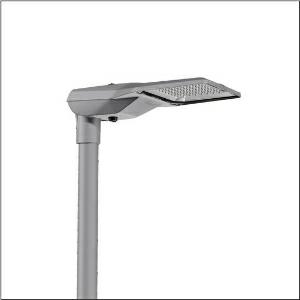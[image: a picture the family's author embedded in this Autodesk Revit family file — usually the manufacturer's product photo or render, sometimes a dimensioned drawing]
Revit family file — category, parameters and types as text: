
# Revit family: streetlight_sl_21_iq_midi___p0_8ab_5xe3r31y08nb_1d5a
name_source: partatom
category: Lighting Fixtures
units: mm (PartAtom-declared; Revit-internal decimal feet)

## family parameters
Cut with Voids When Loaded = No
Host = Face
Light Source = No
Part Type = Normal
Room Calculation Point = No
Round Connector Dimension = Use Diameter
Shared = No

## types (1)
- --- (1 x LED, 18710 lm, 136.6 W, 3000K)
    Apparent Load = 137 VA
    CIE Flux Codes = 39 72 97 100 100
    Color Rendering = 70
    Color Temperature = 3000K
    Default Elevation = 1800 mm
    Description = Streetlight SL 21 iQ midi, mast luminaire, primary light control with lens, of PMMA, primary optical cover: cover, of toughened safety glass, transparent, light distribution: P0.8aB, light emission: direct distribution, primary light characteristic: asymmetric, installation type: post-top, side-entry, LED, High Power LED, rated luminous flux: 18.710lm, luminous efficacy: 137lm/W, light colour: 730, colour temperature: 3000K, control gear: iQ-Street Remote, D4i with power reduction, control: pre-setting: logarithmic dimming characteristic, Street-Remote, Auto-Match, Temp-Guard, Lumen-Switch, Night-Set, Smart-Wire, Light-Fading, Desk-Remote (wireless, voltage-free reading and setting of iQ features in the workshop via application-optimized NFC function/RFID function), optimised constant luminous flux control (CLO 2.0), mains connection: 230..240V, AC, 50/60Hz, start of lifetime: 137W, end of service life: 144W, reduction: 61W, luminaire housing, of diecast aluminium, powder-coated, SITECO metallic grey (DB 702S), corrosivity category C5 high according to DIN EN ISO 12944, please order mast flange separately, inclination adjustable: 0°, 5°, 10°, 15°, sealing non-destructively replaceable, multi-level sealing system, length: 644mm, width: 335mm, height: 110mm, mast flange for spigot size: 42mm (side-entry): 5XC10008XM4, 60/48mm (side-entry/post-top): 5XC10108XM2, 76/60mm (side-entry/post-top): 5XC10108XM1, mounting height: 4..8m, Smart Interface below and above, protection rating (complete): IP66, insulation class (complete): insulation class II (safety insulation), certification: CE, ENEC, ENEC+, VDE, impact resistance: IK10, permissible operating ambient temperature for outdoor applications: -40..+50°C, standard-compliant lighting for roads and squares, packaging unit: 1 piece

Light Distribution: P0.8aB
    Height = 111 mm
    Lamp = 1 x LED
    Lamp Light Flux = 18710 lm
    Lamp Power = 136.6 W
    Lamp count = 1
    Length = 644 mm
    Luminous efficacy = 137 lm/W
    Manufacturer = Siteco
    ModVariant = No
    Model = 5XE3R31Y08NB
    Number of Poles = 1
    OnlyDefault = Yes
    Power Factor = 1
    Product Name = Streetlight SL 21 iQ midi | P0.8aB
    Product group = mast luminaire | pylon top
    ProductGroupID = 6100
    Protection Class = Protection class II
    Protection Degree = IP 66
    RLX_Detail_Level = 1
    RLX_Emergency_Light_Flux = 0 lm
    RLX_Emergency_Type = 0
    RLX_Emergency_Type_DB = No
    RlxData = <blob elided: 90665 chars, md5=81f62f97>
    Socket = socket
    Standby Power = 0 W
    System Light Flux = 18710 lm
    System Power = 137 W
    Type Comments = factory setting: luminous flux: 100 % | dim-lin: 254 | 733 mA
    Type Image = l_1004304.jpg
    URL = http://relux.com
    VarID = @adj_078915
    Voltage = 0 V
    Weight = 0.00 kg
    Width = 336 mm

## geometry (parser evidence)
native form markers: Blend x4, Sweep x9
no freeform markers — native parametric forms only
